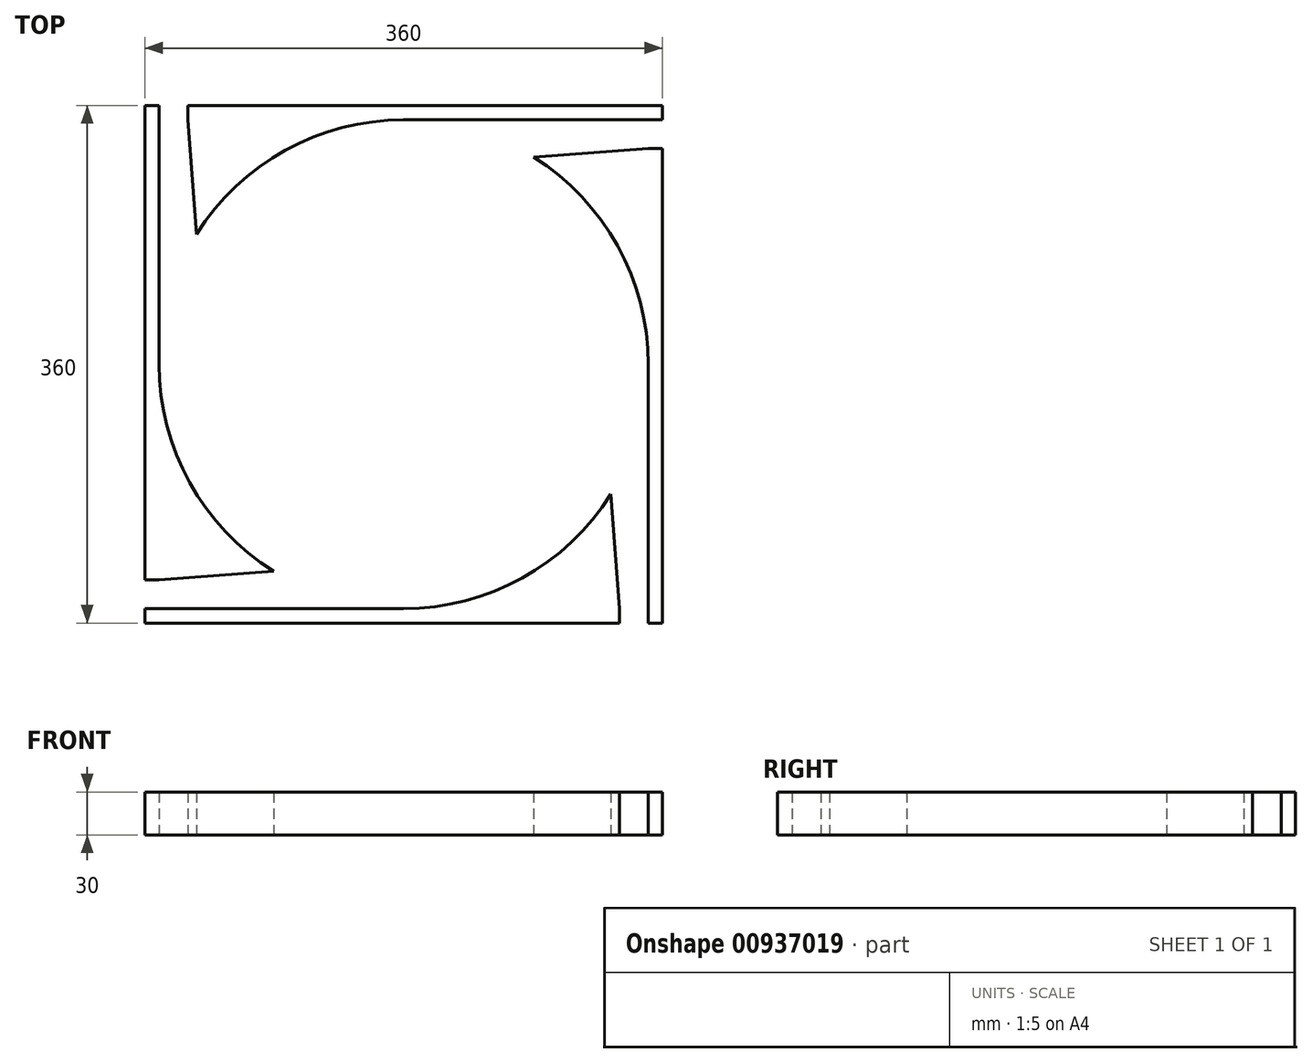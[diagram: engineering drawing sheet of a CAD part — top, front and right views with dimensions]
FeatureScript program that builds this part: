
annotation { "Feature Type Name" : "Feature", "Feature Type Description" : "" }
export const myFeature = defineFeature(function(context is Context, id is Id, definition is map)
    precondition{}
    {
        {
            var Q0;
            Q0=qCreatedBy(makeId("Top.planeOp"),FACE);
            var sketch = newSketch(context, id + "F0", { "sketchPlane" : qUnion([Q0])});
            skLineSegment(sketch, "E0.bottom", {"start": v(-345, -345) * mm, "end": v(345, -345) * mm, "construction": true});
            skLineSegment(sketch, "E0.top", {"start": v(-345, 345) * mm, "end": v(345, 345) * mm, "construction": true});
            skLineSegment(sketch, "E0.left", {"start": v(-345, -345) * mm, "end": v(-345, 345) * mm, "construction": true});
            skLineSegment(sketch, "E0.right", {"start": v(345, -345) * mm, "end": v(345, 345) * mm, "construction": true});
            skLineSegment(sketch, "E1.bottom", {"start": v(-115, 115) * mm, "end": v(115, 115) * mm, "construction": true});
            skLineSegment(sketch, "E1.top", {"start": v(-115, -115) * mm, "end": v(115, -115) * mm, "construction": true});
            skLineSegment(sketch, "E1.left", {"start": v(-115, 115) * mm, "end": v(-115, -115) * mm, "construction": true});
            skLineSegment(sketch, "E1.right", {"start": v(115, 115) * mm, "end": v(115, -115) * mm, "construction": true});
            skLineSegment(sketch, "E2.bottom", {"start": v(-245, 170) * mm, "end": v(-219, 170) * mm, "construction": true});
            skLineSegment(sketch, "E2.top", {"start": v(-245, -170) * mm, "end": v(-219, -170) * mm, "construction": true});
            skLineSegment(sketch, "E2.left", {"start": v(-245, 170) * mm, "end": v(-245, -170) * mm, "construction": true});
            skLineSegment(sketch, "E2.right", {"start": v(-219, 170) * mm, "end": v(-219, -170) * mm, "construction": true});
            skLineSegment(sketch, "E3.1.0", {"start": v(170, 245) * mm, "end": v(-170, 245) * mm, "construction": true});
            skLineSegment(sketch, "E3.1.1", {"start": v(170, 219) * mm, "end": v(-170, 219) * mm, "construction": true});
            skLineSegment(sketch, "E3.1.2", {"start": v(-170, 245) * mm, "end": v(-170, 219) * mm, "construction": true});
            skLineSegment(sketch, "E3.1.3", {"start": v(170, 245) * mm, "end": v(170, 219) * mm, "construction": true});
            skLineSegment(sketch, "E3.2.0", {"start": v(245, -170) * mm, "end": v(245, 170) * mm, "construction": true});
            skLineSegment(sketch, "E3.2.1", {"start": v(219, -170) * mm, "end": v(219, 170) * mm, "construction": true});
            skLineSegment(sketch, "E3.2.2", {"start": v(245, 170) * mm, "end": v(219, 170) * mm, "construction": true});
            skLineSegment(sketch, "E3.2.3", {"start": v(245, -170) * mm, "end": v(219, -170) * mm, "construction": true});
            skPoint(sketch, "E3.center", {"position": v(0, 0) * mm});
            skLineSegment(sketch, "E4.2.3.0", {"start": v(-170, -245) * mm, "end": v(170, -245) * mm, "construction": true});
            skLineSegment(sketch, "E4.3.3.0", {"start": v(-170, -219) * mm, "end": v(170, -219) * mm, "construction": true});
            skLineSegment(sketch, "E4.6.3.0", {"start": v(170, -245) * mm, "end": v(170, -219) * mm, "construction": true});
            skLineSegment(sketch, "E4.9.3.0", {"start": v(-170, -245) * mm, "end": v(-170, -219) * mm, "construction": true});
            skCircle(sketch, "E5", {"center": v(0, 0) * mm, "radius": 162.63 * mm, "construction": true});
            skSolve(sketch);
        }
        {
            var Q0;
            Q0=qCreatedBy(makeId("Top.planeOp"),FACE);
            var sketch = newSketch(context, id + "F1", { "sketchPlane" : qUnion([Q0])});
            skLineSegment(sketch, "E6.bottom", {"start": v(0, 170) * mm, "end": v(170, 170) * mm});
            skLineSegment(sketch, "E6.top", {"start": v(-170, -170) * mm, "end": v(0, -170) * mm});
            skLineSegment(sketch, "E6.left", {"start": v(-170, 170) * mm, "end": v(-170, 0) * mm});
            skLineSegment(sketch, "E6.right", {"start": v(170, 0) * mm, "end": v(170, -170) * mm});
            skArc(sketch, "E7", {"start": v(-170, 0) * mm, "mid": v(-148.76, -82.28) * mm, "end": v(-90.35, -144) * mm});
            skLineSegment(sketch, "E8", {"start": v(-150, 170) * mm, "end": v(-144, 90.35) * mm});
            skLineSegment(sketch, "E9.1.0", {"start": v(-170, -150) * mm, "end": v(-90.35, -144) * mm});
            skLineSegment(sketch, "E9.2.0", {"start": v(150, -170) * mm, "end": v(144, -90.35) * mm});
            skLineSegment(sketch, "E9.3.0", {"start": v(170, 150) * mm, "end": v(90.35, 144) * mm});
            skArc(sketch, "E10.trimOffspring", {"start": v(0, 170) * mm, "mid": v(-82.28, 148.76) * mm, "end": v(-144, 90.35) * mm});
            skArc(sketch, "E11.trimOffspring", {"start": v(170, 0) * mm, "mid": v(148.76, 82.28) * mm, "end": v(90.35, 144) * mm});
            skArc(sketch, "E12.trimOffspring", {"start": v(0, -170) * mm, "mid": v(82.28, -148.76) * mm, "end": v(144, -90.35) * mm});
            skLineSegment(sketch, "E13", {"start": v(-180, 170) * mm, "end": v(-180, -150) * mm});
            skLineSegment(sketch, "E14", {"start": v(-180, -150) * mm, "end": v(-170, -150) * mm});
            skLineSegment(sketch, "E15.1.1", {"start": v(-170, -180) * mm, "end": v(150, -180) * mm});
            skLineSegment(sketch, "E15.1.2", {"start": v(150, -180) * mm, "end": v(150, -170) * mm});
            skLineSegment(sketch, "E15.2.1", {"start": v(180, -170) * mm, "end": v(180, 150) * mm});
            skLineSegment(sketch, "E15.2.2", {"start": v(180, 150) * mm, "end": v(170, 150) * mm});
            skLineSegment(sketch, "E15.3.1", {"start": v(170, 180) * mm, "end": v(-150, 180) * mm});
            skLineSegment(sketch, "E15.3.2", {"start": v(-150, 180) * mm, "end": v(-150, 170) * mm});
            skLineSegment(sketch, "E16", {"start": v(-170, 170) * mm, "end": v(-170, 180) * mm});
            skLineSegment(sketch, "E17", {"start": v(-170, 180) * mm, "end": v(-180, 180) * mm});
            skLineSegment(sketch, "E18", {"start": v(-180, 180) * mm, "end": v(-180, 170) * mm});
            skLineSegment(sketch, "E19.1.0", {"start": v(-180, -180) * mm, "end": v(-170, -180) * mm});
            skLineSegment(sketch, "E19.1.1", {"start": v(-180, -170) * mm, "end": v(-180, -180) * mm});
            skLineSegment(sketch, "E19.1.2", {"start": v(-170, -170) * mm, "end": v(-180, -170) * mm});
            skLineSegment(sketch, "E19.2.0", {"start": v(180, -180) * mm, "end": v(180, -170) * mm});
            skLineSegment(sketch, "E19.2.1", {"start": v(170, -180) * mm, "end": v(180, -180) * mm});
            skLineSegment(sketch, "E19.2.2", {"start": v(170, -170) * mm, "end": v(170, -180) * mm});
            skLineSegment(sketch, "E19.3.0", {"start": v(180, 180) * mm, "end": v(170, 180) * mm});
            skLineSegment(sketch, "E19.3.1", {"start": v(180, 170) * mm, "end": v(180, 180) * mm});
            skLineSegment(sketch, "E19.3.2", {"start": v(170, 170) * mm, "end": v(180, 170) * mm});
            skSolve(sketch);
        }
        {
            var Q0;
            Q0 = qSketchRegion(id + "F1", true);
            extrude(context, id + "F2", {"entities" : qUnion([Q0]), "depth" : 30 * mm, "offsetDistance" : 25 * mm});
        }
    });
